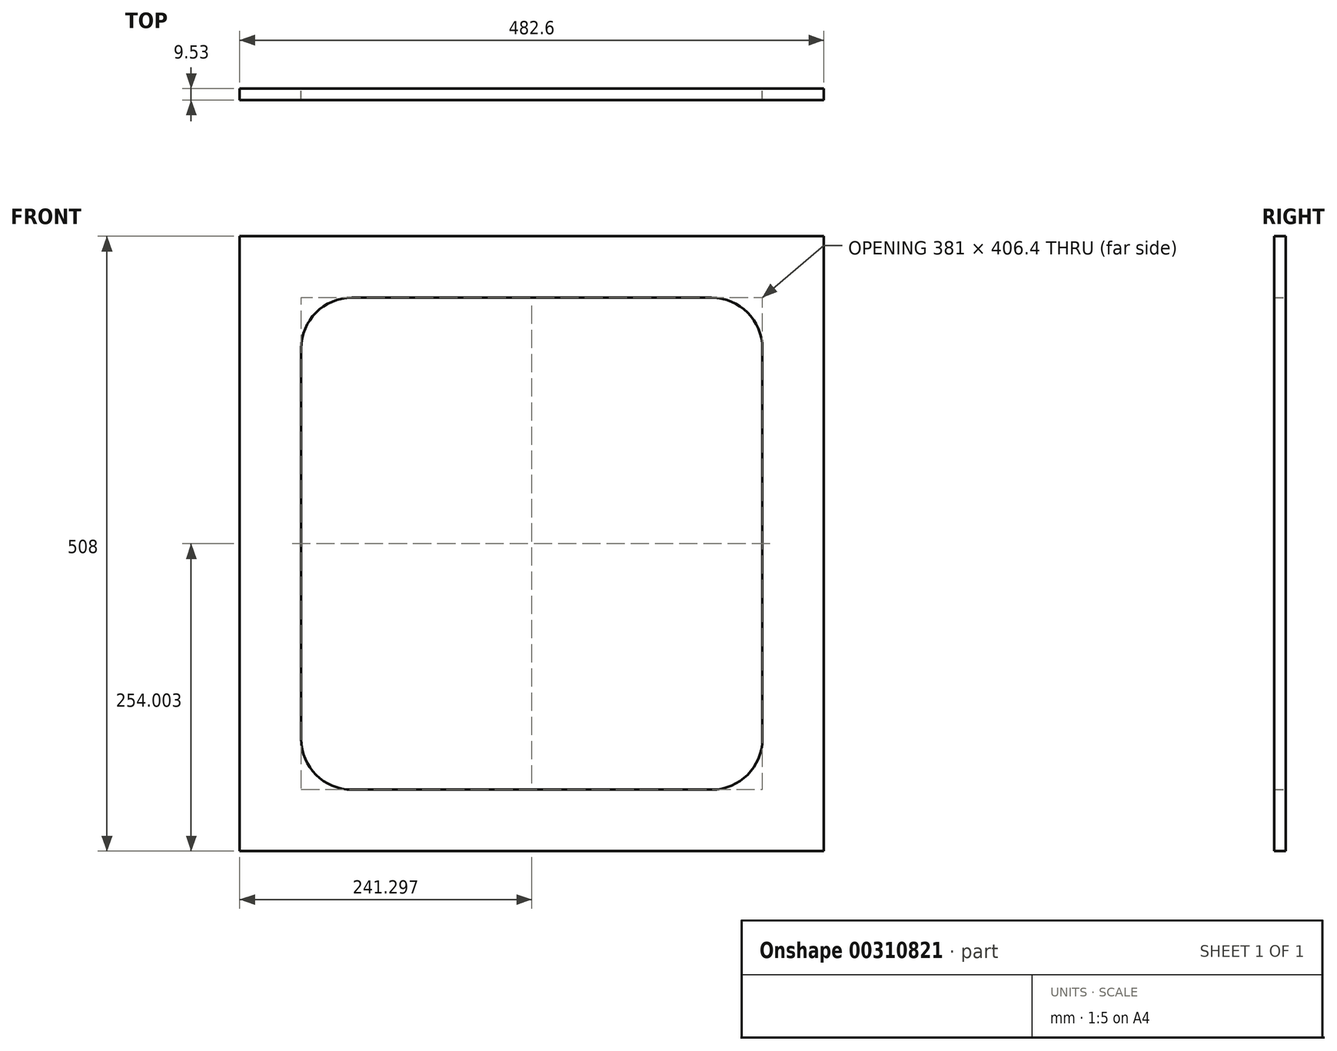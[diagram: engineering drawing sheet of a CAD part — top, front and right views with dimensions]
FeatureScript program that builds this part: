
annotation { "Feature Type Name" : "Feature", "Feature Type Description" : "" }
export const myFeature = defineFeature(function(context is Context, id is Id, definition is map)
    precondition{}
    {
        {
            var Q0;
            Q0=qCreatedBy(makeId("Front.planeOp"),FACE);
            var sketch = newSketch(context, id + "F0", { "sketchPlane" : qUnion([Q0])});
            skLineSegment(sketch, "E0.bottom", {"start": v(-296.5, 588.81) * mm, "end": v(186.1, 588.81) * mm});
            skLineSegment(sketch, "E0.top", {"start": v(-296.5, 80.81) * mm, "end": v(186.1, 80.81) * mm});
            skLineSegment(sketch, "E0.left", {"start": v(-296.5, 588.81) * mm, "end": v(-296.5, 80.81) * mm});
            skLineSegment(sketch, "E0.right", {"start": v(186.1, 588.81) * mm, "end": v(186.1, 80.81) * mm});
            skLineSegment(sketch, "E1.bottom", {"start": v(93.39, 131.61) * mm, "end": v(-203.8, 131.61) * mm});
            skLineSegment(sketch, "E1.top", {"start": v(93.39, 538.01) * mm, "end": v(-203.8, 538.01) * mm});
            skLineSegment(sketch, "E1.left", {"start": v(135.3, 173.52) * mm, "end": v(135.3, 496.1) * mm});
            skLineSegment(sketch, "E1.right", {"start": v(-245.7, 173.52) * mm, "end": v(-245.7, 496.1) * mm});
            skPoint(sketch, "E1.middle", {"position": v(-55.2, 334.81) * mm});
            skPoint(sketch, "E1.middle.positionSnap0", {"position": v(-55.2, 80.81) * mm});
            skPoint(sketch, "E1.middle.positionSnap1", {"position": v(186.1, 334.81) * mm});
            skPoint(sketch, "E1.centerSnap0", {"position": v(-55.2, 80.81) * mm});
            skPoint(sketch, "E1.centerSnap1", {"position": v(186.1, 334.81) * mm});
            skPoint(sketch, "E2.visualSharp", {"position": v(-245.7, 538.01) * mm});
            skArc(sketch, "E2.filletArc", {"start": v(-203.8, 538.01) * mm, "mid": v(-233.43, 525.74) * mm, "end": v(-245.7, 496.1) * mm});
            skPoint(sketch, "E3.visualSharp", {"position": v(-245.7, 131.61) * mm});
            skArc(sketch, "E3.filletArc", {"start": v(-245.7, 173.52) * mm, "mid": v(-233.43, 143.89) * mm, "end": v(-203.8, 131.61) * mm});
            skPoint(sketch, "E4.visualSharp", {"position": v(135.3, 131.61) * mm});
            skArc(sketch, "E4.filletArc", {"start": v(93.39, 131.61) * mm, "mid": v(123.02, 143.89) * mm, "end": v(135.3, 173.52) * mm});
            skPoint(sketch, "E5.visualSharp", {"position": v(135.3, 538.01) * mm});
            skArc(sketch, "E5.filletArc", {"start": v(135.3, 496.1) * mm, "mid": v(123.02, 525.74) * mm, "end": v(93.39, 538.01) * mm});
            skSolve(sketch);
        }
        {
            var Q0;
            Q0=makeQuery(id+"F0.imprint","IMPRINT",FACE,{"disambiguationData":[TD([[makeQuery(id+"F0.imprint","IMPRINT",EDGE,{"derivedFrom":sQuery(id+"F0.wireOp",EDGE,"E0.bottom")}),-1.0]])]});
            extrude(context, id + "F1", {"entities" : qUnion([Q0]), "depth" : 9.52 * mm});
        }
        {
            var Q0;
            Q0=makeQuery(id+"F1.opExtrude","SWEPT_BODY",BODY,{"disambiguationData":[OSD([sQuery(id+"F0.wireOp",EDGE,"E0.bottom"),sQuery(id+"F0.wireOp",EDGE,"E0.top"),sQuery(id+"F0.wireOp",EDGE,"E0.left"),sQuery(id+"F0.wireOp",EDGE,"E0.right"),sQuery(id+"F0.wireOp",EDGE,"E1.bottom"),sQuery(id+"F0.wireOp",EDGE,"E1.top"),sQuery(id+"F0.wireOp",EDGE,"E1.left"),sQuery(id+"F0.wireOp",EDGE,"E1.right"),sQuery(id+"F0.wireOp",EDGE,"E2.filletArc"),sQuery(id+"F0.wireOp",EDGE,"E3.filletArc"),sQuery(id+"F0.wireOp",EDGE,"E4.filletArc"),sQuery(id+"F0.wireOp",EDGE,"E5.filletArc")])]});
            transform(context, id + "F2", {"entities" : qUnion([Q0]), "transformType" : TransformType.TRANSLATION_3D, "dx" : 0 * mm, "dy" : 482.6 * mm, "dz" : 0 * mm, "makeCopy" : true});
        }
        {
            var Q0;
            Q0=makeQuery(id+"F2.opPattern","COPY",BODY,{"derivedFrom":makeQuery(id+"F1.opExtrude","SWEPT_BODY",BODY,{"disambiguationData":[OSD([sQuery(id+"F0.wireOp",EDGE,"E0.bottom"),sQuery(id+"F0.wireOp",EDGE,"E0.top"),sQuery(id+"F0.wireOp",EDGE,"E0.left"),sQuery(id+"F0.wireOp",EDGE,"E0.right"),sQuery(id+"F0.wireOp",EDGE,"E1.bottom"),sQuery(id+"F0.wireOp",EDGE,"E1.top"),sQuery(id+"F0.wireOp",EDGE,"E1.left"),sQuery(id+"F0.wireOp",EDGE,"E1.right"),sQuery(id+"F0.wireOp",EDGE,"E2.filletArc"),sQuery(id+"F0.wireOp",EDGE,"E3.filletArc"),sQuery(id+"F0.wireOp",EDGE,"E4.filletArc"),sQuery(id+"F0.wireOp",EDGE,"E5.filletArc")])]}),"instanceName":"1"});
            deleteBodies(context, id + "F3", {"entities" : qUnion([Q0])});
        }
    });
